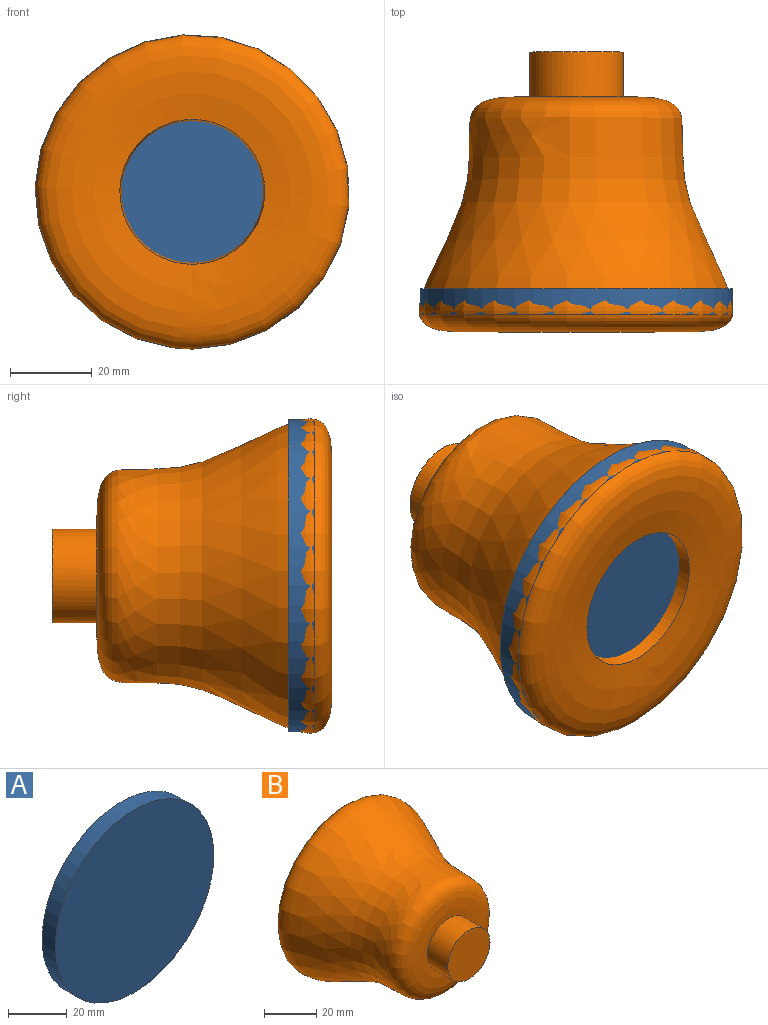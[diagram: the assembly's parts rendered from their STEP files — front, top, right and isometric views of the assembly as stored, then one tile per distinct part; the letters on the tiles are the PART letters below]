
ASSEMBLY  parts=2 mates=1
PART A: 3 faces, bbox 76.2x6.4x76.2 mm
  f0: cylinder r=38.1mm len=76.2mm, axis (0,1,0), area 1520.1mm2, adj f1,f2
  f1: plane 76.2x76.2mm, normal (0,-1,0), area 4560.4mm2, adj f0
  f2: plane 76.2x76.2mm, normal (0,1,0), area 4560.4mm2, adj f0
PART B: 6 faces, bbox 76.6x68.3x76.6 mm
  f0: cylinder r=11.43mm len=22.86mm, axis (0,1,0), area 792.3mm2, adj f1,f2
  f1: plane 22.86x22.86mm, normal (0,-1,0), area 410.4mm2, adj f0
  f2: revolved ~76.63x76.63mm, area 15794.9mm2, adj f0,f3
  f3: cone r=17.68mm half-angle=7.1deg, axis (0,1,0), area 4598.7mm2, adj f2,f5
  f4: plane 22.86x22.86mm, normal (0,1,0), area 410.4mm2, adj f5
  f5: cylinder r=11.43mm len=27.02mm, axis (0,1,0), area 1940.2mm2, adj f3,f4
PLACE A rot(axis=(1,0,0),180deg) t=(-26.96,26.32,-10.99)mm
PLACE B rot(axis=(1,0,0),180deg) t=(-26.96,46.03,-10.99)mm
MATE slider A.f0 <-> B.f0  axis (0,1,0) through (-26.96,32.67,-10.99)mm
